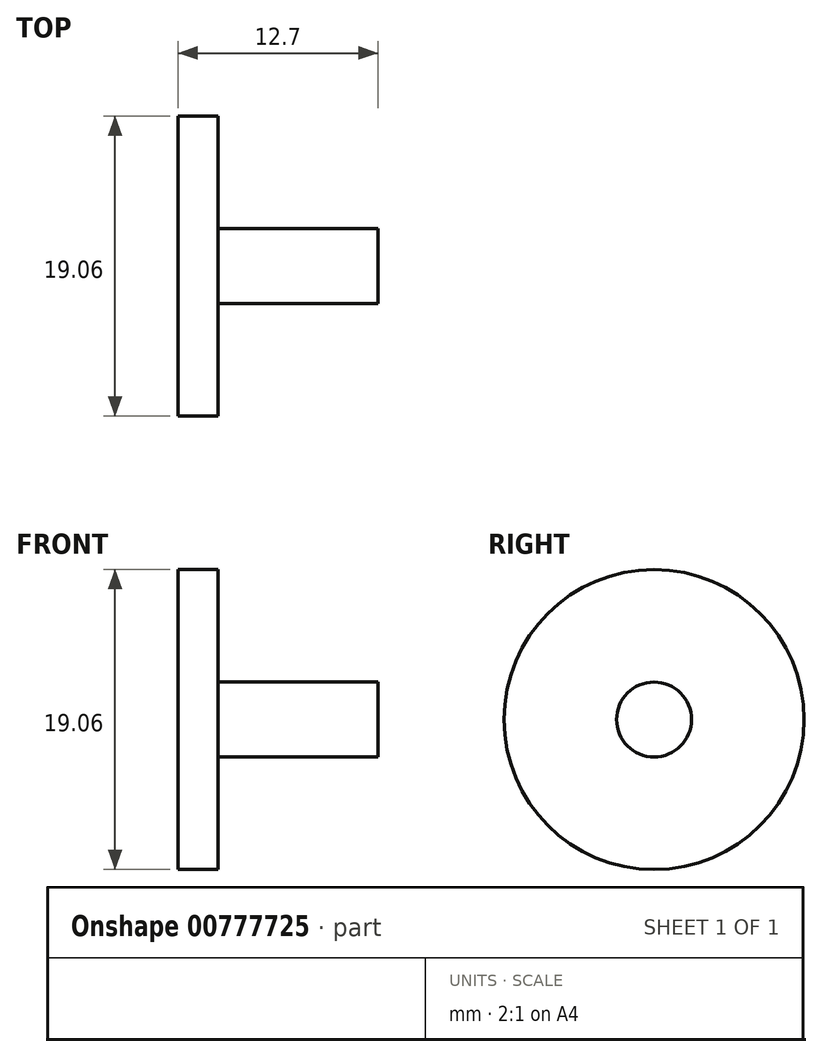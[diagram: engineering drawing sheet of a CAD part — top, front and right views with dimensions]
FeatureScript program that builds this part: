
annotation { "Feature Type Name" : "Feature", "Feature Type Description" : "" }
export const myFeature = defineFeature(function(context is Context, id is Id, definition is map)
    precondition{}
    {
        {
            var Q0;
            Q0=qCreatedBy(makeId("Front.planeOp"),FACE);
            var sketch = newSketch(context, id + "F0", { "sketchPlane" : qUnion([Q0])});
            skLineSegment(sketch, "E0.top", {"start": v(0, 9.53) * mm, "end": v(2.54, 9.53) * mm});
            skLineSegment(sketch, "E0.left", {"start": v(0, 0) * mm, "end": v(0, 9.53) * mm});
            skLineSegment(sketch, "E0.right", {"start": v(2.54, 2.38) * mm, "end": v(2.54, 9.53) * mm});
            skLineSegment(sketch, "E1.bottom", {"start": v(0, 0) * mm, "end": v(12.7, 0) * mm});
            skLineSegment(sketch, "E1.top", {"start": v(2.54, 2.38) * mm, "end": v(12.7, 2.38) * mm});
            skLineSegment(sketch, "E1.right", {"start": v(12.7, 0) * mm, "end": v(12.7, 2.38) * mm});
            skSolve(sketch);
        }
        {
            var Q0;
            Q0 = qSketchRegion(id + "F0", true);
            var Q1;
            Q1=sQuery(id+"F0.wireOp",EDGE,"E1.bottom");
            revolve(context, id + "F1", {"surfaceOperationType" : NewSurfaceOperationType.NEW, "entities" : qUnion([Q0]), "axis" : qUnion([Q1]), "revolveType" : RevolveType.FULL});
        }
    });
